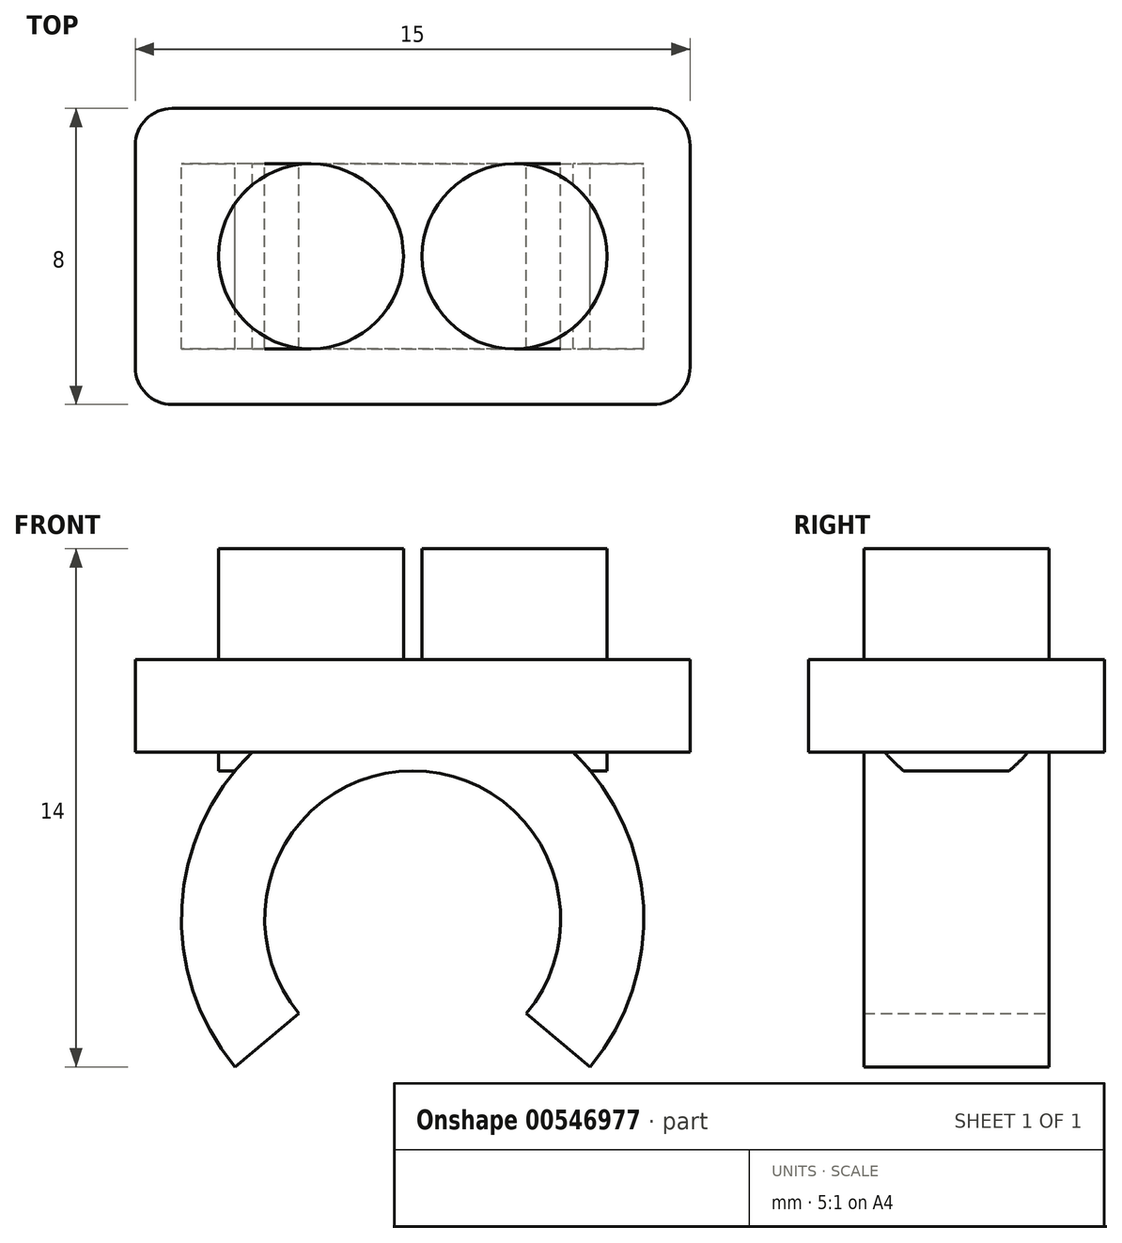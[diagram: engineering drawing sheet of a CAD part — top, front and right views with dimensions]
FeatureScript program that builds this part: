
annotation { "Feature Type Name" : "Feature", "Feature Type Description" : "" }
export const myFeature = defineFeature(function(context is Context, id is Id, definition is map)
    precondition{}
    {
        {
            var Q0;
            Q0=qCreatedBy(makeId("Top.planeOp"),FACE);
            var sketch = newSketch(context, id + "F0", { "sketchPlane" : qUnion([Q0])});
            skCircle(sketch, "E0", {"center": v(2.75, 0) * mm, "radius": 2.5 * mm});
            skCircle(sketch, "E1", {"center": v(-2.75, 0) * mm, "radius": 2.5 * mm});
            skSolve(sketch);
        }
        {
            var Q0;
            Q0=makeQuery(id+"F0.imprint","IMPRINT",FACE,{"disambiguationData":[TD([[makeQuery(id+"F0.imprint","IMPRINT",EDGE,{"derivedFrom":sQuery(id+"F0.wireOp",EDGE,"E1")}),1.0]])]});
            var Q1;
            Q1=makeQuery(id+"F0.imprint","IMPRINT",FACE,{"disambiguationData":[TD([[makeQuery(id+"F0.imprint","IMPRINT",EDGE,{"derivedFrom":sQuery(id+"F0.wireOp",EDGE,"E0")}),1.0]])]});
            extrude(context, id + "F1", {"entities" : qUnion([Q0, Q1]), "endBound" : BoundingType.SYMMETRIC, "oppositeDirection" : true, "depth" : 6 * mm, "offsetDistance" : 25 * mm});
        }
        {
            var Q0;
            Q0=qCreatedBy(makeId("Top.planeOp"),FACE);
            var sketch = newSketch(context, id + "F2", { "sketchPlane" : qUnion([Q0])});
            skLineSegment(sketch, "E2.bottom", {"start": v(7.5, -4) * mm, "end": v(-7.5, -4) * mm});
            skLineSegment(sketch, "E2.top", {"start": v(7.5, 4) * mm, "end": v(-7.5, 4) * mm});
            skLineSegment(sketch, "E2.left", {"start": v(7.5, -4) * mm, "end": v(7.5, 4) * mm});
            skLineSegment(sketch, "E2.right", {"start": v(-7.5, -4) * mm, "end": v(-7.5, 4) * mm});
            skPoint(sketch, "E2.middle", {"position": v(0, 0) * mm});
            skSolve(sketch);
        }
        {
            var Q0;
            Q0=makeQuery(id+"F2.imprint","IMPRINT",FACE,{"disambiguationData":[TD([[makeQuery(id+"F2.imprint","IMPRINT",EDGE,{"derivedFrom":sQuery(id+"F2.wireOp",EDGE,"E2.bottom")}),-1.0]])]});
            extrude(context, id + "F3", {"entities" : qUnion([Q0]), "oppositeDirection" : true, "depth" : 2.5 * mm, "offsetDistance" : 25 * mm});
        }
        {
            var Q0;
            Q0=qCreatedBy(makeId("Front.planeOp"),FACE);
            var sketch = newSketch(context, id + "F4", { "sketchPlane" : qUnion([Q0])});
            skArc(sketch, "E3", {"start": v(3.07, -9.56) * mm, "mid": v(0, -3) * mm, "end": v(-3.07, -9.56) * mm});
            skArc(sketch, "E4", {"start": v(4.8, -11) * mm, "mid": v(0, -0.75) * mm, "end": v(-4.8, -11) * mm});
            skLineSegment(sketch, "E5", {"start": v(-3.07, -9.56) * mm, "end": v(-4.8, -11) * mm});
            skLineSegment(sketch, "E6", {"start": v(3.07, -9.56) * mm, "end": v(4.8, -11) * mm});
            skSolve(sketch);
        }
        {
            var Q0;
            Q0 = qSketchRegion(id + "F4", true);
            extrude(context, id + "F5", {"entities" : qUnion([Q0]), "operationType" : NewBodyOperationType.ADD, "endBound" : BoundingType.SYMMETRIC, "depth" : 5 * mm, "offsetDistance" : 25 * mm});
        }
        {
            var Q0;
            Q0=makeQuery(id+"F3.opExtrude","SWEPT_EDGE",EDGE,{"disambiguationData":[OSD([sQuery(id+"F2.wireOp",EDGE,"E2.bottom"),sQuery(id+"F2.wireOp",EDGE,"E2.left")])]});
            var Q1;
            Q1=makeQuery(id+"F3.opExtrude","SWEPT_EDGE",EDGE,{"disambiguationData":[OSD([sQuery(id+"F2.wireOp",EDGE,"E2.bottom"),sQuery(id+"F2.wireOp",EDGE,"E2.right")])]});
            var Q2;
            Q2=makeQuery(id+"F3.opExtrude","SWEPT_EDGE",EDGE,{"disambiguationData":[OSD([sQuery(id+"F2.wireOp",EDGE,"E2.top"),sQuery(id+"F2.wireOp",EDGE,"E2.left")])]});
            var Q3;
            Q3=makeQuery(id+"F3.opExtrude","SWEPT_EDGE",EDGE,{"disambiguationData":[OSD([sQuery(id+"F2.wireOp",EDGE,"E2.top"),sQuery(id+"F2.wireOp",EDGE,"E2.right")])]});
            fillet(context, id + "F6", {"entities" : qUnion([Q0, Q1, Q2, Q3]), "radius" : 1 * mm, "tangentPropagation" : true, "allowEdgeOverflow" : false});
        }
    });
